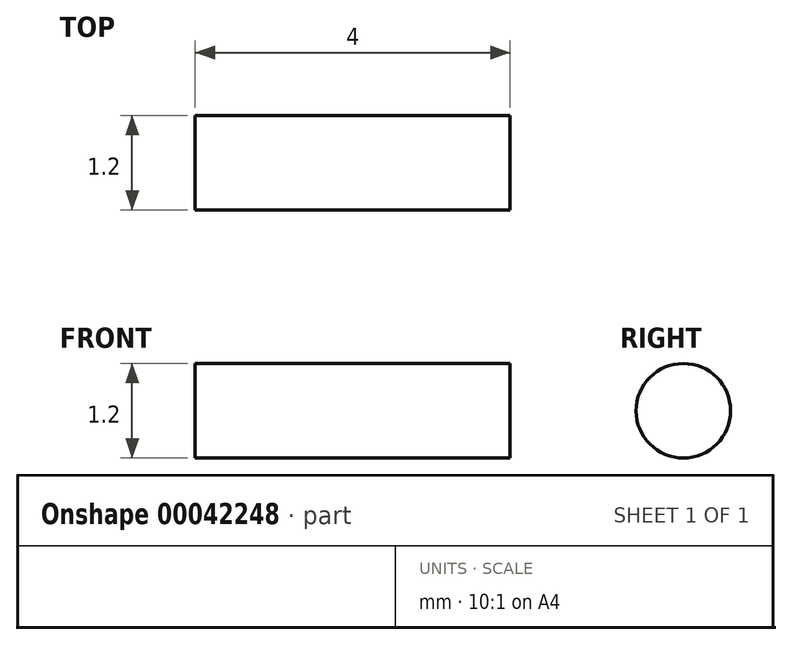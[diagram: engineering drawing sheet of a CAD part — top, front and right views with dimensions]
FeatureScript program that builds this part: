
annotation { "Feature Type Name" : "Feature", "Feature Type Description" : "" }
export const myFeature = defineFeature(function(context is Context, id is Id, definition is map)
    precondition{}
    {
        {
            var Q0;
            Q0=qCreatedBy(makeId("Right.planeOp"),FACE);
            var sketch = newSketch(context, id + "F0", { "sketchPlane" : qUnion([Q0])});
            skCircle(sketch, "E0", {"center": v(0, 0) * mm, "radius": 0.6 * mm});
            skSolve(sketch);
        }
        {
            var Q0;
            Q0 = qSketchRegion(id + "F0", true);
            extrude(context, id + "F1", {"entities" : qUnion([Q0]), "depth" : 4 * mm});
        }
    });
